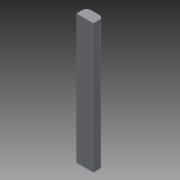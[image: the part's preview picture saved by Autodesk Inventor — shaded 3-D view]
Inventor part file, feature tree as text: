
AUTODESK INVENTOR PART (.ipt)
format: ipt  version: 2013 (Build 170138000, 138)  size: 73,728 bytes
history: native  units: in
note: dims shown in document units (in); Inventor stores cm internally (conversion verified against a paired STEP export)
features: extrude x1, fillet x1, sketch x1
ambient origin geometry x8: Origin, YZ Plane, XZ Plane, XY Plane, X Axis, Y Axis, Z Axis, Center Point
bodies: Solid1 (feature_tree)
feature tree (3):
  extrude  "Extrusion1"  Depth=3.0in
  fillet  "Fillet1"  Radius=5.0in
  sketch  "Sketch1"  dims[d0=5.0in d1=3.0in d2=5.0in d3=38.0in d4=3.0in d5=0.0in d6=1.25in]
